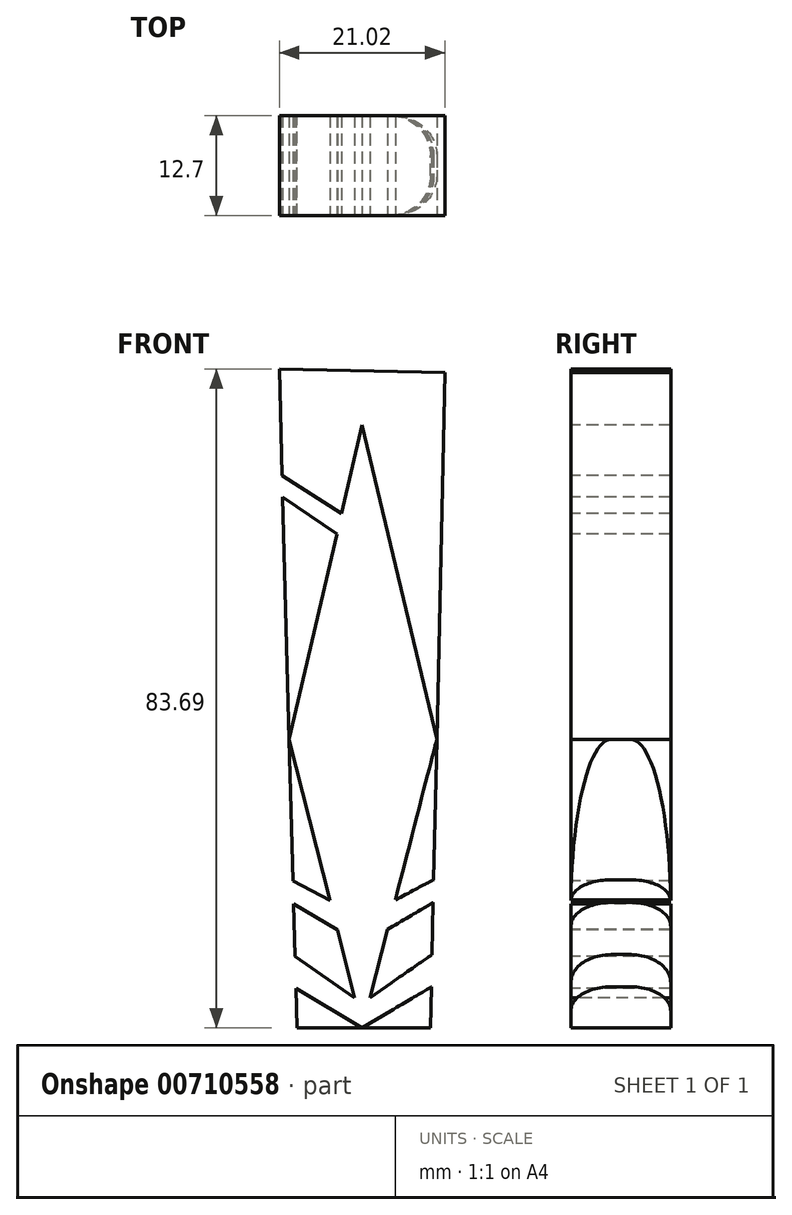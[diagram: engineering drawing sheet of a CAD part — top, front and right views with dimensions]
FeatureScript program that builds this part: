
annotation { "Feature Type Name" : "Feature", "Feature Type Description" : "" }
export const myFeature = defineFeature(function(context is Context, id is Id, definition is map)
    precondition{}
    {
        {
            var Q0;
            Q0=qCreatedBy(makeId("Front.planeOp"),FACE);
            var sketch = newSketch(context, id + "F0", { "sketchPlane" : qUnion([Q0])});
            skLineSegment(sketch, "E0", {"start": v(0, -8.4) * mm, "end": v(-10.52, -8.17) * mm});
            skLineSegment(sketch, "E1", {"start": v(-10.52, -8.17) * mm, "end": v(10.5, -8.63) * mm});
            skLineSegment(sketch, "E2", {"start": v(10.5, -8.63) * mm, "end": v(0, -8.4) * mm});
            skLineSegment(sketch, "E3", {"start": v(-10.52, -8.17) * mm, "end": v(-8.3, -91.86) * mm});
            skLineSegment(sketch, "E4", {"start": v(-8.3, -91.86) * mm, "end": v(-10.52, -8.17) * mm});
            skLineSegment(sketch, "E5", {"start": v(10.5, -8.63) * mm, "end": v(8.67, -91.86) * mm});
            skLineSegment(sketch, "E6", {"start": v(8.67, -91.86) * mm, "end": v(-8.3, -91.86) * mm});
            skSolve(sketch);
        }
        {
            var Q0;
            Q0=makeQuery(id+"F0.imprint","IMPRINT",FACE,{"disambiguationData":[TD([[makeQuery(id+"F0.imprint","IMPRINT",EDGE,{"derivedFrom":sQuery(id+"F0.wireOp",EDGE,"E1")}),-1.0]])]});
            extrude(context, id + "F1", {"entities" : qUnion([Q0]), "depth" : 6.35 * mm, "offsetDistance" : 25.4 * mm});
        }
        {
            var Q0;
            Q0=makeQuery(id+"F1.opExtrude","CAP_FACE",FACE,{"disambiguationData":[OSD([sQuery(id+"F0.wireOp",EDGE,"E1"),sQuery(id+"F0.wireOp",EDGE,"E2"),sQuery(id+"F0.wireOp",EDGE,"E4"),sQuery(id+"F0.wireOp",EDGE,"E5"),sQuery(id+"F0.wireOp",EDGE,"E6")])],"isStart":true});
            extrude(context, id + "F2", {"entities" : qUnion([Q0]), "operationType" : NewBodyOperationType.ADD, "depth" : 6.35 * mm, "offsetDistance" : 25.4 * mm});
        }
        {
            var Q0;
            Q0=makeQuery(id+"F1.opExtrude","CAP_FACE",FACE,{"disambiguationData":[OSD([sQuery(id+"F0.wireOp",EDGE,"E1"),sQuery(id+"F0.wireOp",EDGE,"E2"),sQuery(id+"F0.wireOp",EDGE,"E4"),sQuery(id+"F0.wireOp",EDGE,"E5"),sQuery(id+"F0.wireOp",EDGE,"E6")])],"isStart":false});
            var sketch = newSketch(context, id + "F3", { "sketchPlane" : qUnion([Q0])});
            skLineSegment(sketch, "E7", {"start": v(0, -12.7) * mm, "end": v(-8.4, -8.21) * mm});
            skLineSegment(sketch, "E8", {"start": v(-8.4, -8.21) * mm, "end": v(0, -12.7) * mm});
            skLineSegment(sketch, "E9", {"start": v(0, -15.3) * mm, "end": v(-10.47, -10.2) * mm});
            skLineSegment(sketch, "E10", {"start": v(-10.47, -10.2) * mm, "end": v(0, -15.3) * mm});
            skLineSegment(sketch, "E11", {"start": v(0, -15.3) * mm, "end": v(-9.27, -55.2) * mm});
            skLineSegment(sketch, "E12", {"start": v(-9.27, -55.2) * mm, "end": v(0, -91.86) * mm});
            skLineSegment(sketch, "E13", {"start": v(0, -91.86) * mm, "end": v(9.48, -55.2) * mm});
            skLineSegment(sketch, "E14", {"start": v(9.48, -55.2) * mm, "end": v(0, -15.3) * mm});
            skLineSegment(sketch, "E15", {"start": v(2.66, -26.5) * mm, "end": v(10.21, -21.68) * mm});
            skLineSegment(sketch, "E16", {"start": v(10.21, -21.68) * mm, "end": v(2.66, -26.5) * mm});
            skLineSegment(sketch, "E17", {"start": v(3.27, -29.07) * mm, "end": v(10.15, -24.4) * mm});
            skLineSegment(sketch, "E18", {"start": v(0, -91.86) * mm, "end": v(8.78, -86.64) * mm});
            skLineSegment(sketch, "E19", {"start": v(1, -88.02) * mm, "end": v(8.87, -82.55) * mm});
            skLineSegment(sketch, "E20", {"start": v(4.2, -75.62) * mm, "end": v(9.08, -73.04) * mm});
            skLineSegment(sketch, "E21", {"start": v(3.23, -79.36) * mm, "end": v(9.02, -75.93) * mm});
            skLineSegment(sketch, "E22", {"start": v(0, -44.6) * mm, "end": v(0, -50.7) * mm});
            skLineSegment(sketch, "E23.MirrorCS", {"start": v(-10.21, -21.68) * mm, "end": v(-2.66, -26.5) * mm});
            skLineSegment(sketch, "E24.MirrorCS", {"start": v(-3.27, -29.07) * mm, "end": v(-10.15, -24.4) * mm});
            skLineSegment(sketch, "E25.MirrorCS", {"start": v(10.47, -10.2) * mm, "end": v(0, -15.3) * mm});
            skLineSegment(sketch, "E26.MirrorCS", {"start": v(8.4, -8.21) * mm, "end": v(0, -12.7) * mm});
            skLineSegment(sketch, "E27.MirrorCS", {"start": v(-4.2, -75.62) * mm, "end": v(-9.08, -73.04) * mm});
            skLineSegment(sketch, "E28.MirrorCS", {"start": v(-3.23, -79.36) * mm, "end": v(-9.02, -75.93) * mm});
            skLineSegment(sketch, "E29.MirrorCS", {"start": v(-1, -88.02) * mm, "end": v(-8.87, -82.55) * mm});
            skLineSegment(sketch, "E30.MirrorCS", {"start": v(0, -91.86) * mm, "end": v(-8.78, -86.64) * mm});
            skLineSegment(sketch, "E31", {"start": v(-3.46, -28.94) * mm, "end": v(-3.21, -29.1) * mm});
            skLineSegment(sketch, "E32", {"start": v(-2.67, -26.5) * mm, "end": v(-2.61, -26.53) * mm});
            skLineSegment(sketch, "E33", {"start": v(-4.27, -75.58) * mm, "end": v(-4.1, -75.67) * mm});
            skLineSegment(sketch, "E34", {"start": v(-3.31, -79.31) * mm, "end": v(-3.15, -79.4) * mm});
            skLineSegment(sketch, "E35", {"start": v(-1, -88.01) * mm, "end": v(-0.97, -88.04) * mm});
            skSolve(sketch);
        }
        {
            var Q0;
            {var subQ7=sQuery(id+"F3.wireOp",EDGE,"E35");var subQ9=makeQuery(id+"F3.imprint","IMPRINT",VERTEX,{"derivedFrom":subQ7});Q0=makeQuery(id+"F3.imprint","IMPRINT",FACE,{"disambiguationData":[TD([[makeQuery(id+"F3.imprint","IMPRINT",EDGE,{"disambiguationData":[TD([[subQ9,1.0]])],"derivedFrom":subQ7}),-1.0]])]});}
            var Q1;
            {var subQ0=sQuery(id+"F3.wireOp",EDGE,"E33");var subQ3=makeQuery(id+"F3.imprint","IMPRINT",VERTEX,{"derivedFrom":subQ0});Q1=makeQuery(id+"F3.imprint","IMPRINT",FACE,{"disambiguationData":[TD([[makeQuery(id+"F3.imprint","IMPRINT",EDGE,{"disambiguationData":[TD([[subQ3,1.0]])],"derivedFrom":subQ0}),-1.0]])]});}
            var Q2;
            {var subQ0=sQuery(id+"F3.wireOp",EDGE,"E20");Q2=makeQuery(id+"F3.imprint","IMPRINT",FACE,{"disambiguationData":[TD([[makeQuery(id+"F3.imprint","IMPRINT",EDGE,{"derivedFrom":subQ0}),-1.0]])]});}
            var Q3;
            {var subQ0=sQuery(id+"F3.wireOp",EDGE,"E18");Q3=makeQuery(id+"F3.imprint","IMPRINT",FACE,{"disambiguationData":[TD([[makeQuery(id+"F3.imprint","IMPRINT",EDGE,{"derivedFrom":subQ0}),1.0]])]});}
            var Q4;
            {var subQ0=sQuery(id+"F3.wireOp",EDGE,"E16");Q4=makeQuery(id+"F3.imprint","IMPRINT",FACE,{"disambiguationData":[TD([[makeQuery(id+"F3.imprint","IMPRINT",EDGE,{"derivedFrom":subQ0}),1.0]])]});}
            var Q5;
            {var subQ10=sQuery(id+"F3.wireOp",EDGE,"E11");var subQ13=makeQuery(id+"F3.imprint","INTERSECT",VERTEX,{"derivedFrom":[subQ10,sQuery(id+"F3.wireOp",EDGE,"E31")]});Q5=makeQuery(id+"F3.imprint","IMPRINT",FACE,{"disambiguationData":[TD([[makeQuery(id+"F3.imprint","IMPRINT",EDGE,{"disambiguationData":[TD([[subQ13,1.0]])],"derivedFrom":subQ10}),1.0]])]});}
            var Q6;
            {var subQ0=sQuery(id+"F3.wireOp",EDGE,"E31");var subQ3=makeQuery(id+"F3.imprint","IMPRINT",VERTEX,{"derivedFrom":subQ0});Q6=makeQuery(id+"F3.imprint","IMPRINT",FACE,{"disambiguationData":[TD([[makeQuery(id+"F3.imprint","IMPRINT",EDGE,{"disambiguationData":[TD([[subQ3,1.0]])],"derivedFrom":subQ0}),1.0]])]});}
            var Q7;
            {var subQ5=sQuery(id+"F3.wireOp",EDGE,"E8");Q7=makeQuery(id+"F3.imprint","IMPRINT",FACE,{"disambiguationData":[TD([[makeQuery(id+"F3.imprint","IMPRINT",EDGE,{"derivedFrom":subQ5}),-1.0]])]});}
            extrude(context, id + "F4", {"entities" : qUnion([Q0, Q1, Q2, Q3, Q4, Q5, Q6, Q7]), "operationType" : NewBodyOperationType.REMOVE, "oppositeDirection" : true, "depth" : 25.4 * mm, "offsetDistance" : 25.4 * mm});
        }
        {
            var Q0;
            {var subQ0=sQuery(id+"F0.wireOp",EDGE,"E4");Q0=makeQuery(id+"F4.boolean.opBoolean","SPLIT",EDGE,{"disambiguationData":[TD([makeQuery(id+"F4.opExtrude","SWEPT_FACE",FACE,{"disambiguationData":[OSD([sQuery(id+"F3.wireOp",EDGE,"E10")])]})])],"derivedFrom":makeQuery(id+"F1.opExtrude","CAP_EDGE",EDGE,{"disambiguationData":[OSD([subQ0])],"isStart":false})});}
            var Q1;
            {var subQ1=sQuery(id+"F0.wireOp",EDGE,"E4");var subQ2=makeQuery(id+"F1.opExtrude","CAP_EDGE",EDGE,{"disambiguationData":[OSD([subQ1])],"isStart":false});var subQ3=sQuery(id+"F3.wireOp",EDGE,"E31");Q1=makeQuery(id+"F4.boolean.opBoolean","SPLIT",EDGE,{"disambiguationData":[TD([makeQuery(id+"F4.opExtrude","SWEPT_FACE",FACE,{"disambiguationData":[OSD([sQuery(id+"F3.wireOp",EDGE,"E24.MirrorCS"),subQ3])]})])],"derivedFrom":subQ2});}
            var Q2;
            {var subQ1=sQuery(id+"F0.wireOp",EDGE,"E4");var subQ2=makeQuery(id+"F1.opExtrude","CAP_EDGE",EDGE,{"disambiguationData":[OSD([subQ1])],"isStart":false});var subQ3=sQuery(id+"F3.wireOp",EDGE,"E33");Q2=makeQuery(id+"F4.boolean.opBoolean","SPLIT",EDGE,{"disambiguationData":[TD([makeQuery(id+"F4.opExtrude","SWEPT_FACE",FACE,{"disambiguationData":[OSD([sQuery(id+"F3.wireOp",EDGE,"E27.MirrorCS"),subQ3])]})])],"derivedFrom":subQ2});}
            var Q3;
            {var subQ0=sQuery(id+"F0.wireOp",EDGE,"E4");Q3=makeQuery(id+"F4.boolean.opBoolean","SPLIT",EDGE,{"disambiguationData":[TD([makeQuery(id+"F4.opExtrude","SWEPT_FACE",FACE,{"disambiguationData":[OSD([sQuery(id+"F3.wireOp",EDGE,"E28.MirrorCS"),sQuery(id+"F3.wireOp",EDGE,"E34")])]})])],"derivedFrom":makeQuery(id+"F1.opExtrude","CAP_EDGE",EDGE,{"disambiguationData":[OSD([subQ0])],"isStart":false})});}
            var Q4;
            {var subQ0=sQuery(id+"F0.wireOp",EDGE,"E6");var subQ1=sQuery(id+"F0.wireOp",EDGE,"E4");Q4=makeQuery(id+"F4.boolean.opBoolean","SPLIT",EDGE,{"disambiguationData":[TD([makeQuery(id+"F1.opExtrude","SWEPT_FACE",FACE,{"disambiguationData":[OSD([subQ0])]})])],"derivedFrom":makeQuery(id+"F1.opExtrude","CAP_EDGE",EDGE,{"disambiguationData":[OSD([subQ1])],"isStart":false})});}
            var Q5;
            {var subQ0=sQuery(id+"F0.wireOp",EDGE,"E5");var subQ1=sQuery(id+"F0.wireOp",EDGE,"E6");Q5=makeQuery(id+"F4.boolean.opBoolean","SPLIT",EDGE,{"disambiguationData":[TD([makeQuery(id+"F1.opExtrude","SWEPT_FACE",FACE,{"disambiguationData":[OSD([subQ1])]})])],"derivedFrom":makeQuery(id+"F1.opExtrude","CAP_EDGE",EDGE,{"disambiguationData":[OSD([subQ0])],"isStart":false})});}
            var Q6;
            {var subQ0=sQuery(id+"F0.wireOp",EDGE,"E5");Q6=makeQuery(id+"F4.boolean.opBoolean","SPLIT",EDGE,{"disambiguationData":[TD([makeQuery(id+"F4.opExtrude","SWEPT_FACE",FACE,{"disambiguationData":[OSD([sQuery(id+"F3.wireOp",EDGE,"E19")])]})])],"derivedFrom":makeQuery(id+"F1.opExtrude","CAP_EDGE",EDGE,{"disambiguationData":[OSD([subQ0])],"isStart":false})});}
            var Q7;
            {var subQ0=sQuery(id+"F0.wireOp",EDGE,"E5");var subQ2=makeQuery(id+"F1.opExtrude","CAP_EDGE",EDGE,{"disambiguationData":[OSD([subQ0])],"isStart":false});var subQ3=sQuery(id+"F3.wireOp",EDGE,"E20");Q7=makeQuery(id+"F4.boolean.opBoolean","SPLIT",EDGE,{"disambiguationData":[TD([makeQuery(id+"F4.opExtrude","SWEPT_FACE",FACE,{"disambiguationData":[OSD([subQ3])]})])],"derivedFrom":subQ2});}
            var Q8;
            {var subQ1=sQuery(id+"F0.wireOp",EDGE,"E5");var subQ2=makeQuery(id+"F1.opExtrude","CAP_EDGE",EDGE,{"disambiguationData":[OSD([subQ1])],"isStart":false});var subQ3=sQuery(id+"F3.wireOp",EDGE,"E17");Q8=makeQuery(id+"F4.boolean.opBoolean","SPLIT",EDGE,{"disambiguationData":[TD([makeQuery(id+"F4.opExtrude","SWEPT_FACE",FACE,{"disambiguationData":[OSD([subQ3])]})])],"derivedFrom":subQ2});}
            var Q9;
            {var subQ0=sQuery(id+"F0.wireOp",EDGE,"E5");Q9=makeQuery(id+"F4.boolean.opBoolean","SPLIT",EDGE,{"disambiguationData":[TD([makeQuery(id+"F4.opExtrude","SWEPT_FACE",FACE,{"disambiguationData":[OSD([sQuery(id+"F3.wireOp",EDGE,"E16")])]})])],"derivedFrom":makeQuery(id+"F1.opExtrude","CAP_EDGE",EDGE,{"disambiguationData":[OSD([subQ0])],"isStart":false})});}
            var Q10;
            {var subQ0=sQuery(id+"F0.wireOp",EDGE,"E5");Q10=makeQuery(id+"F4.boolean.opBoolean","SPLIT",EDGE,{"disambiguationData":[TD([makeQuery(id+"F4.opExtrude","SWEPT_FACE",FACE,{"disambiguationData":[OSD([sQuery(id+"F3.wireOp",EDGE,"E16")])]})])],"derivedFrom":makeQuery(id+"F2.opExtrude","CAP_EDGE",EDGE,{"disambiguationData":[OSD([subQ0])],"isStart":false})});}
            var Q11;
            {var subQ0=sQuery(id+"F0.wireOp",EDGE,"E5");var subQ2=sQuery(id+"F3.wireOp",EDGE,"E17");Q11=makeQuery(id+"F4.boolean.opBoolean","SPLIT",EDGE,{"disambiguationData":[TD([makeQuery(id+"F4.opExtrude","SWEPT_FACE",FACE,{"disambiguationData":[OSD([subQ2])]})])],"derivedFrom":makeQuery(id+"F2.opExtrude","CAP_EDGE",EDGE,{"disambiguationData":[OSD([subQ0])],"isStart":false})});}
            var Q12;
            {var subQ1=sQuery(id+"F0.wireOp",EDGE,"E5");var subQ2=sQuery(id+"F3.wireOp",EDGE,"E20");Q12=makeQuery(id+"F4.boolean.opBoolean","SPLIT",EDGE,{"disambiguationData":[TD([makeQuery(id+"F4.opExtrude","SWEPT_FACE",FACE,{"disambiguationData":[OSD([subQ2])]})])],"derivedFrom":makeQuery(id+"F2.opExtrude","CAP_EDGE",EDGE,{"disambiguationData":[OSD([subQ1])],"isStart":false})});}
            var Q13;
            {var subQ0=sQuery(id+"F0.wireOp",EDGE,"E5");Q13=makeQuery(id+"F4.boolean.opBoolean","SPLIT",EDGE,{"disambiguationData":[TD([makeQuery(id+"F4.opExtrude","SWEPT_FACE",FACE,{"disambiguationData":[OSD([sQuery(id+"F3.wireOp",EDGE,"E19")])]})])],"derivedFrom":makeQuery(id+"F2.opExtrude","CAP_EDGE",EDGE,{"disambiguationData":[OSD([subQ0])],"isStart":false})});}
            var Q14;
            {var subQ0=sQuery(id+"F0.wireOp",EDGE,"E5");var subQ1=sQuery(id+"F0.wireOp",EDGE,"E6");Q14=makeQuery(id+"F4.boolean.opBoolean","SPLIT",EDGE,{"disambiguationData":[TD([makeQuery(id+"F1.opExtrude","SWEPT_FACE",FACE,{"disambiguationData":[OSD([subQ1])]})])],"derivedFrom":makeQuery(id+"F2.opExtrude","CAP_EDGE",EDGE,{"disambiguationData":[OSD([subQ0])],"isStart":false})});}
            var Q15;
            {var subQ0=sQuery(id+"F0.wireOp",EDGE,"E6");var subQ1=sQuery(id+"F0.wireOp",EDGE,"E4");Q15=makeQuery(id+"F4.boolean.opBoolean","SPLIT",EDGE,{"disambiguationData":[TD([makeQuery(id+"F1.opExtrude","SWEPT_FACE",FACE,{"disambiguationData":[OSD([subQ0])]})])],"derivedFrom":makeQuery(id+"F2.opExtrude","CAP_EDGE",EDGE,{"disambiguationData":[OSD([subQ1])],"isStart":false})});}
            var Q16;
            {var subQ0=sQuery(id+"F0.wireOp",EDGE,"E4");Q16=makeQuery(id+"F4.boolean.opBoolean","SPLIT",EDGE,{"disambiguationData":[TD([makeQuery(id+"F4.opExtrude","SWEPT_FACE",FACE,{"disambiguationData":[OSD([sQuery(id+"F3.wireOp",EDGE,"E28.MirrorCS"),sQuery(id+"F3.wireOp",EDGE,"E34")])]})])],"derivedFrom":makeQuery(id+"F2.opExtrude","CAP_EDGE",EDGE,{"disambiguationData":[OSD([subQ0])],"isStart":false})});}
            var Q17;
            {var subQ1=sQuery(id+"F0.wireOp",EDGE,"E4");var subQ2=sQuery(id+"F3.wireOp",EDGE,"E33");Q17=makeQuery(id+"F4.boolean.opBoolean","SPLIT",EDGE,{"disambiguationData":[TD([makeQuery(id+"F4.opExtrude","SWEPT_FACE",FACE,{"disambiguationData":[OSD([sQuery(id+"F3.wireOp",EDGE,"E27.MirrorCS"),subQ2])]})])],"derivedFrom":makeQuery(id+"F2.opExtrude","CAP_EDGE",EDGE,{"disambiguationData":[OSD([subQ1])],"isStart":false})});}
            var Q18;
            {var subQ0=sQuery(id+"F0.wireOp",EDGE,"E4");var subQ2=sQuery(id+"F3.wireOp",EDGE,"E31");Q18=makeQuery(id+"F4.boolean.opBoolean","SPLIT",EDGE,{"disambiguationData":[TD([makeQuery(id+"F4.opExtrude","SWEPT_FACE",FACE,{"disambiguationData":[OSD([sQuery(id+"F3.wireOp",EDGE,"E24.MirrorCS"),subQ2])]})])],"derivedFrom":makeQuery(id+"F2.opExtrude","CAP_EDGE",EDGE,{"disambiguationData":[OSD([subQ0])],"isStart":false})});}
            var Q19;
            {var subQ0=sQuery(id+"F0.wireOp",EDGE,"E4");Q19=makeQuery(id+"F4.boolean.opBoolean","SPLIT",EDGE,{"disambiguationData":[TD([makeQuery(id+"F4.opExtrude","SWEPT_FACE",FACE,{"disambiguationData":[OSD([sQuery(id+"F3.wireOp",EDGE,"E10")])]})])],"derivedFrom":makeQuery(id+"F2.opExtrude","CAP_EDGE",EDGE,{"disambiguationData":[OSD([subQ0])],"isStart":false})});}
            fillet(context, id + "F5", {"entities" : qUnion([Q0, Q1, Q2, Q3, Q4, Q5, Q6, Q7, Q8, Q9, Q10, Q11, Q12, Q13, Q14, Q15, Q16, Q17, Q18, Q19]), "radius" : 5.08 * mm, "tangentPropagation" : true, "allowEdgeOverflow" : false});
        }
    });
